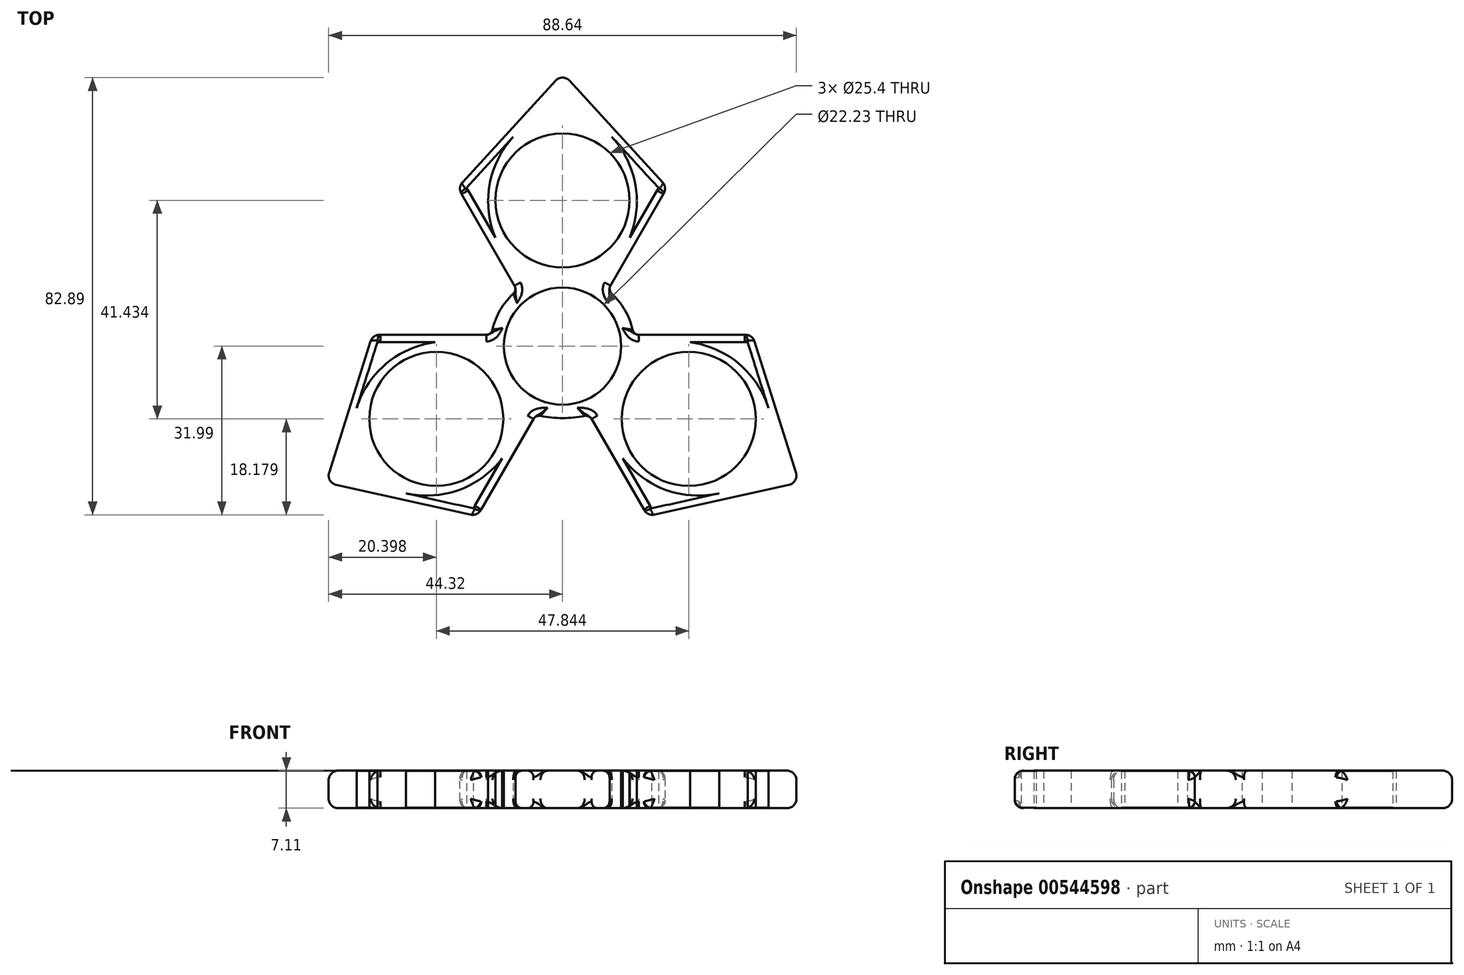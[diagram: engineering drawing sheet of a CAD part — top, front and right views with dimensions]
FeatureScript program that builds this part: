
annotation { "Feature Type Name" : "Feature", "Feature Type Description" : "" }
export const myFeature = defineFeature(function(context is Context, id is Id, definition is map)
    precondition{}
    {
        {
            var Q0;
            Q0=qCreatedBy(makeId("Top.planeOp"),FACE);
            var sketch = newSketch(context, id + "F0", { "sketchPlane" : qUnion([Q0])});
            skCircle(sketch, "E0", {"center": v(0, 0) * mm, "radius": 11.11 * mm});
            skCircle(sketch, "E1", {"center": v(0, 27.62) * mm, "radius": 12.7 * mm});
            skCircle(sketch, "E2", {"center": v(-23.92, -13.81) * mm, "radius": 12.7 * mm});
            skCircle(sketch, "E3", {"center": v(23.92, -13.81) * mm, "radius": 12.7 * mm});
            skLineSegment(sketch, "E4", {"start": v(-10.9, 2.14) * mm, "end": v(-35.98, 2.14) * mm});
            skLineSegment(sketch, "E5", {"start": v(0, 0) * mm, "end": v(-23.92, -13.81) * mm});
            skLineSegment(sketch, "E6", {"start": v(0, 0) * mm, "end": v(23.92, -13.81) * mm});
            skLineSegment(sketch, "E7", {"start": v(0, 0) * mm, "end": v(0, 27.62) * mm});
            skLineSegment(sketch, "E8.MirrorCS", {"start": v(-3.6, -10.51) * mm, "end": v(-16.13, -32.23) * mm});
            skLineSegment(sketch, "E9.MirrorCS", {"start": v(7.3, 8.37) * mm, "end": v(19.85, 30.09) * mm});
            skLineSegment(sketch, "E10.MirrorCS", {"start": v(-7.3, 8.37) * mm, "end": v(-19.85, 30.09) * mm});
            skLineSegment(sketch, "E11.MirrorCS", {"start": v(3.6, -10.51) * mm, "end": v(16.13, -32.23) * mm});
            skLineSegment(sketch, "E12.MirrorCS", {"start": v(10.9, 2.14) * mm, "end": v(35.98, 2.14) * mm});
            skLineSegment(sketch, "E13", {"start": v(0, 0) * mm, "end": v(-49.05, -28.32) * mm});
            skLineSegment(sketch, "E14", {"start": v(-35.98, 2.14) * mm, "end": v(-44.82, -25.88) * mm});
            skLineSegment(sketch, "E15", {"start": v(-44.82, -25.88) * mm, "end": v(-16.13, -32.23) * mm});
            skLineSegment(sketch, "E16", {"start": v(0, 0) * mm, "end": v(0, 57.4) * mm});
            skLineSegment(sketch, "E17", {"start": v(0, 0) * mm, "end": v(62.97, -36.36) * mm});
            skLineSegment(sketch, "E18", {"start": v(16.13, -32.23) * mm, "end": v(44.82, -25.88) * mm});
            skLineSegment(sketch, "E19", {"start": v(44.82, -25.88) * mm, "end": v(35.98, 2.14) * mm});
            skLineSegment(sketch, "E20", {"start": v(19.85, 30.09) * mm, "end": v(0, 51.75) * mm});
            skLineSegment(sketch, "E21", {"start": v(0, 51.75) * mm, "end": v(-19.85, 30.09) * mm});
            skLineSegment(sketch, "E22", {"start": v(-9.34, 39.66) * mm, "end": v(-18.18, 30.01) * mm});
            skLineSegment(sketch, "E23", {"start": v(-18.18, 30.01) * mm, "end": v(-12.73, 20.56) * mm});
            skArc(sketch, "E24", {"start": v(-9.34, 39.66) * mm, "mid": v(-13.81, 30.6) * mm, "end": v(-12.73, 20.56) * mm});
            skArc(sketch, "E25.MirrorCS", {"start": v(9.34, 39.66) * mm, "mid": v(13.81, 30.6) * mm, "end": v(12.73, 20.56) * mm});
            skLineSegment(sketch, "E26.MirrorCS", {"start": v(9.34, 39.66) * mm, "end": v(18.18, 30.01) * mm});
            skLineSegment(sketch, "E27.MirrorCS", {"start": v(18.18, 30.01) * mm, "end": v(12.73, 20.56) * mm});
            skLineSegment(sketch, "E28.MirrorCS", {"start": v(16.9, -30.75) * mm, "end": v(11.44, -21.3) * mm});
            skLineSegment(sketch, "E29.MirrorCS", {"start": v(29.68, -27.92) * mm, "end": v(16.9, -30.75) * mm});
            skArc(sketch, "E30.MirrorCS", {"start": v(29.68, -27.92) * mm, "mid": v(19.6, -27.27) * mm, "end": v(11.44, -21.3) * mm});
            skArc(sketch, "E31.MirrorCS", {"start": v(39.02, -11.74) * mm, "mid": v(33.41, -3.34) * mm, "end": v(24.17, 0.74) * mm});
            skLineSegment(sketch, "E32.MirrorCS", {"start": v(39.02, -11.74) * mm, "end": v(35.08, 0.74) * mm});
            skLineSegment(sketch, "E33.MirrorCS", {"start": v(35.08, 0.74) * mm, "end": v(24.17, 0.74) * mm});
            skLineSegment(sketch, "E34.MirrorCS", {"start": v(-39.02, -11.74) * mm, "end": v(-35.08, 0.74) * mm});
            skArc(sketch, "E35.MirrorCS", {"start": v(-39.02, -11.74) * mm, "mid": v(-33.41, -3.34) * mm, "end": v(-24.17, 0.74) * mm});
            skLineSegment(sketch, "E36.MirrorCS", {"start": v(-35.08, 0.74) * mm, "end": v(-24.17, 0.74) * mm});
            skLineSegment(sketch, "E37.MirrorCS", {"start": v(-29.68, -27.92) * mm, "end": v(-16.9, -30.75) * mm});
            skArc(sketch, "E38.MirrorCS", {"start": v(-29.68, -27.92) * mm, "mid": v(-19.6, -27.27) * mm, "end": v(-11.44, -21.3) * mm});
            skLineSegment(sketch, "E39.MirrorCS", {"start": v(-16.9, -30.75) * mm, "end": v(-11.44, -21.3) * mm});
            skArc(sketch, "E40", {"start": v(-8.58, 10.57) * mm, "mid": v(-11.82, 6.83) * mm, "end": v(-13.44, 2.14) * mm});
            skArc(sketch, "E41", {"start": v(13.44, 2.14) * mm, "mid": v(11.82, 6.83) * mm, "end": v(8.58, 10.57) * mm});
            skArc(sketch, "E42", {"start": v(-5.06, -13.05) * mm, "mid": v(0, -13.65) * mm, "end": v(5.06, -13.05) * mm});
            skSolve(sketch);
        }
        {
            var Q0;
            {var subQ8=sQuery(id+"F0.wireOp",EDGE,"E21");Q0=makeQuery(id+"F0.imprint","IMPRINT",FACE,{"disambiguationData":[TD([[makeQuery(id+"F0.imprint","IMPRINT",EDGE,{"derivedFrom":subQ8}),1.0]])]});}
            var Q1;
            {var subQ4=sQuery(id+"F0.wireOp",EDGE,"E20");Q1=makeQuery(id+"F0.imprint","IMPRINT",FACE,{"disambiguationData":[TD([[makeQuery(id+"F0.imprint","IMPRINT",EDGE,{"derivedFrom":subQ4}),1.0]])]});}
            var Q2;
            {var subQ5=sQuery(id+"F0.wireOp",EDGE,"E41");Q2=makeQuery(id+"F0.imprint","IMPRINT",FACE,{"disambiguationData":[TD([[makeQuery(id+"F0.imprint","IMPRINT",EDGE,{"derivedFrom":subQ5}),1.0]])]});}
            var Q3;
            {var subQ5=sQuery(id+"F0.wireOp",EDGE,"E40");Q3=makeQuery(id+"F0.imprint","IMPRINT",FACE,{"disambiguationData":[TD([[makeQuery(id+"F0.imprint","IMPRINT",EDGE,{"derivedFrom":subQ5}),1.0]])]});}
            var Q4;
            {var subQ5=sQuery(id+"F0.wireOp",EDGE,"E42");Q4=makeQuery(id+"F0.imprint","IMPRINT",FACE,{"disambiguationData":[TD([[makeQuery(id+"F0.imprint","IMPRINT",EDGE,{"derivedFrom":subQ5}),1.0]])]});}
            var Q5;
            {var subQ6=sQuery(id+"F0.wireOp",EDGE,"E14");Q5=makeQuery(id+"F0.imprint","IMPRINT",FACE,{"disambiguationData":[TD([[makeQuery(id+"F0.imprint","IMPRINT",EDGE,{"derivedFrom":subQ6}),1.0]])]});}
            var Q6;
            {var subQ0=sQuery(id+"F0.wireOp",EDGE,"E15");Q6=makeQuery(id+"F0.imprint","IMPRINT",FACE,{"disambiguationData":[TD([[makeQuery(id+"F0.imprint","IMPRINT",EDGE,{"derivedFrom":subQ0}),1.0]])]});}
            var Q7;
            {var subQ0=sQuery(id+"F0.wireOp",EDGE,"E18");Q7=makeQuery(id+"F0.imprint","IMPRINT",FACE,{"disambiguationData":[TD([[makeQuery(id+"F0.imprint","IMPRINT",EDGE,{"derivedFrom":subQ0}),1.0]])]});}
            var Q8;
            {var subQ0=sQuery(id+"F0.wireOp",EDGE,"E19");Q8=makeQuery(id+"F0.imprint","IMPRINT",FACE,{"disambiguationData":[TD([[makeQuery(id+"F0.imprint","IMPRINT",EDGE,{"derivedFrom":subQ0}),1.0]])]});}
            extrude(context, id + "F1", {"entities" : qUnion([Q0, Q1, Q2, Q3, Q4, Q5, Q6, Q7, Q8]), "depth" : 7.11 * mm, "offsetDistance" : 25.4 * mm});
        }
        {
            var Q0;
            Q0=makeQuery(id+"F1.opExtrude","CAP_EDGE",EDGE,{"disambiguationData":[OSD([sQuery(id+"F0.wireOp",EDGE,"E21")])],"isStart":false});
            var Q1;
            Q1=makeQuery(id+"F1.opExtrude","CAP_EDGE",EDGE,{"disambiguationData":[OSD([sQuery(id+"F0.wireOp",EDGE,"E20")])],"isStart":false});
            var Q2;
            Q2=makeQuery(id+"F1.opExtrude","CAP_EDGE",EDGE,{"disambiguationData":[OSD([sQuery(id+"F0.wireOp",EDGE,"E14")])],"isStart":false});
            var Q3;
            Q3=makeQuery(id+"F1.opExtrude","CAP_EDGE",EDGE,{"disambiguationData":[OSD([sQuery(id+"F0.wireOp",EDGE,"E15")])],"isStart":false});
            var Q4;
            Q4=makeQuery(id+"F1.opExtrude","CAP_EDGE",EDGE,{"disambiguationData":[OSD([sQuery(id+"F0.wireOp",EDGE,"E18")])],"isStart":false});
            var Q5;
            Q5=makeQuery(id+"F1.opExtrude","CAP_EDGE",EDGE,{"disambiguationData":[OSD([sQuery(id+"F0.wireOp",EDGE,"E19")])],"isStart":false});
            var Q6;
            Q6=makeQuery(id+"F1.opExtrude","CAP_EDGE",EDGE,{"disambiguationData":[OSD([sQuery(id+"F0.wireOp",EDGE,"E20")])],"isStart":true});
            var Q7;
            Q7=makeQuery(id+"F1.opExtrude","CAP_EDGE",EDGE,{"disambiguationData":[OSD([sQuery(id+"F0.wireOp",EDGE,"E21")])],"isStart":true});
            var Q8;
            Q8=makeQuery(id+"F1.opExtrude","CAP_EDGE",EDGE,{"disambiguationData":[OSD([sQuery(id+"F0.wireOp",EDGE,"E19")])],"isStart":true});
            var Q9;
            Q9=makeQuery(id+"F1.opExtrude","CAP_EDGE",EDGE,{"disambiguationData":[OSD([sQuery(id+"F0.wireOp",EDGE,"E18")])],"isStart":true});
            var Q10;
            Q10=makeQuery(id+"F1.opExtrude","CAP_EDGE",EDGE,{"disambiguationData":[OSD([sQuery(id+"F0.wireOp",EDGE,"E15")])],"isStart":true});
            var Q11;
            Q11=makeQuery(id+"F1.opExtrude","CAP_EDGE",EDGE,{"disambiguationData":[OSD([sQuery(id+"F0.wireOp",EDGE,"E14")])],"isStart":true});
            var Q12;
            Q12=makeQuery(id+"F1.opExtrude","CAP_EDGE",EDGE,{"disambiguationData":[OSD([sQuery(id+"F0.wireOp",EDGE,"E40")])],"isStart":true});
            var Q13;
            Q13=makeQuery(id+"F1.opExtrude","CAP_EDGE",EDGE,{"disambiguationData":[OSD([sQuery(id+"F0.wireOp",EDGE,"E41")])],"isStart":true});
            var Q14;
            Q14=makeQuery(id+"F1.opExtrude","CAP_EDGE",EDGE,{"disambiguationData":[OSD([sQuery(id+"F0.wireOp",EDGE,"E42")])],"isStart":true});
            var Q15;
            Q15=makeQuery(id+"F1.opExtrude","CAP_EDGE",EDGE,{"disambiguationData":[OSD([sQuery(id+"F0.wireOp",EDGE,"E41")])],"isStart":false});
            var Q16;
            Q16=makeQuery(id+"F1.opExtrude","CAP_EDGE",EDGE,{"disambiguationData":[OSD([sQuery(id+"F0.wireOp",EDGE,"E40")])],"isStart":false});
            var Q17;
            Q17=makeQuery(id+"F1.opExtrude","CAP_EDGE",EDGE,{"disambiguationData":[OSD([sQuery(id+"F0.wireOp",EDGE,"E42")])],"isStart":false});
            var Q18;
            Q18=makeQuery(id+"F1.opExtrude","SWEPT_EDGE",EDGE,{"disambiguationData":[OSD([sQuery(id+"F0.wireOp",EDGE,"E10.MirrorCS"),sQuery(id+"F0.wireOp",EDGE,"E21")])]});
            var Q19;
            Q19=makeQuery(id+"F1.opExtrude","SWEPT_EDGE",EDGE,{"disambiguationData":[OSD([sQuery(id+"F0.wireOp",EDGE,"E13"),sQuery(id+"F0.wireOp",EDGE,"E14"),sQuery(id+"F0.wireOp",EDGE,"E15")])]});
            var Q20;
            Q20=makeQuery(id+"F1.opExtrude","SWEPT_EDGE",EDGE,{"disambiguationData":[OSD([sQuery(id+"F0.wireOp",EDGE,"E4"),sQuery(id+"F0.wireOp",EDGE,"E14")])]});
            var Q21;
            Q21=makeQuery(id+"F1.opExtrude","SWEPT_EDGE",EDGE,{"disambiguationData":[OSD([sQuery(id+"F0.wireOp",EDGE,"E11.MirrorCS"),sQuery(id+"F0.wireOp",EDGE,"E18")])]});
            var Q22;
            Q22=makeQuery(id+"F1.opExtrude","SWEPT_EDGE",EDGE,{"disambiguationData":[OSD([sQuery(id+"F0.wireOp",EDGE,"E17"),sQuery(id+"F0.wireOp",EDGE,"E18"),sQuery(id+"F0.wireOp",EDGE,"E19")])]});
            var Q23;
            Q23=makeQuery(id+"F1.opExtrude","SWEPT_EDGE",EDGE,{"disambiguationData":[OSD([sQuery(id+"F0.wireOp",EDGE,"E8.MirrorCS"),sQuery(id+"F0.wireOp",EDGE,"E15")])]});
            var Q24;
            Q24=makeQuery(id+"F1.opExtrude","SWEPT_EDGE",EDGE,{"disambiguationData":[OSD([sQuery(id+"F0.wireOp",EDGE,"E12.MirrorCS"),sQuery(id+"F0.wireOp",EDGE,"E19")])]});
            var Q25;
            Q25=makeQuery(id+"F1.opExtrude","SWEPT_EDGE",EDGE,{"disambiguationData":[OSD([sQuery(id+"F0.wireOp",EDGE,"E9.MirrorCS"),sQuery(id+"F0.wireOp",EDGE,"E20")])]});
            var Q26;
            Q26=makeQuery(id+"F1.opExtrude","SWEPT_EDGE",EDGE,{"disambiguationData":[OSD([sQuery(id+"F0.wireOp",EDGE,"E16"),sQuery(id+"F0.wireOp",EDGE,"E20"),sQuery(id+"F0.wireOp",EDGE,"E21")])]});
            fillet(context, id + "F2", {"entities" : qUnion([Q0, Q1, Q2, Q3, Q4, Q5, Q6, Q7, Q8, Q9, Q10, Q11, Q12, Q13, Q14, Q15, Q16, Q17, Q18, Q19, Q20, Q21, Q22, Q23, Q24, Q25, Q26]), "radius" : 1.78 * mm, "tangentPropagation" : true, "allowEdgeOverflow" : false});
        }
        {
            var Q0;
            Q0=makeQuery(id+"F1.opExtrude","SWEPT_FACE",FACE,{"disambiguationData":[OSD([sQuery(id+"F0.wireOp",EDGE,"E8.MirrorCS")])]});
            var Q1;
            Q1=makeQuery(id+"F1.opExtrude","SWEPT_FACE",FACE,{"disambiguationData":[OSD([sQuery(id+"F0.wireOp",EDGE,"E9.MirrorCS")])]});
            var Q2;
            Q2=makeQuery(id+"F1.opExtrude","SWEPT_FACE",FACE,{"disambiguationData":[OSD([sQuery(id+"F0.wireOp",EDGE,"E11.MirrorCS")])]});
            var Q3;
            Q3=makeQuery(id+"F1.opExtrude","SWEPT_FACE",FACE,{"disambiguationData":[OSD([sQuery(id+"F0.wireOp",EDGE,"E12.MirrorCS")])]});
            var Q4;
            Q4=makeQuery(id+"F1.opExtrude","SWEPT_FACE",FACE,{"disambiguationData":[OSD([sQuery(id+"F0.wireOp",EDGE,"E10.MirrorCS")])]});
            var Q5;
            Q5=makeQuery(id+"F1.opExtrude","SWEPT_FACE",FACE,{"disambiguationData":[OSD([sQuery(id+"F0.wireOp",EDGE,"E4")])]});
            var Q6;
            Q6=makeQuery(id+"F1.opExtrude","SWEPT_FACE",FACE,{"disambiguationData":[OSD([sQuery(id+"F0.wireOp",EDGE,"E4")])]});
            fillet(context, id + "F3", {"entities" : qUnion([Q0, Q1, Q2, Q3, Q4, Q5, Q6]), "radius" : 1.27 * mm, "tangentPropagation" : true, "allowEdgeOverflow" : false});
        }
    });
